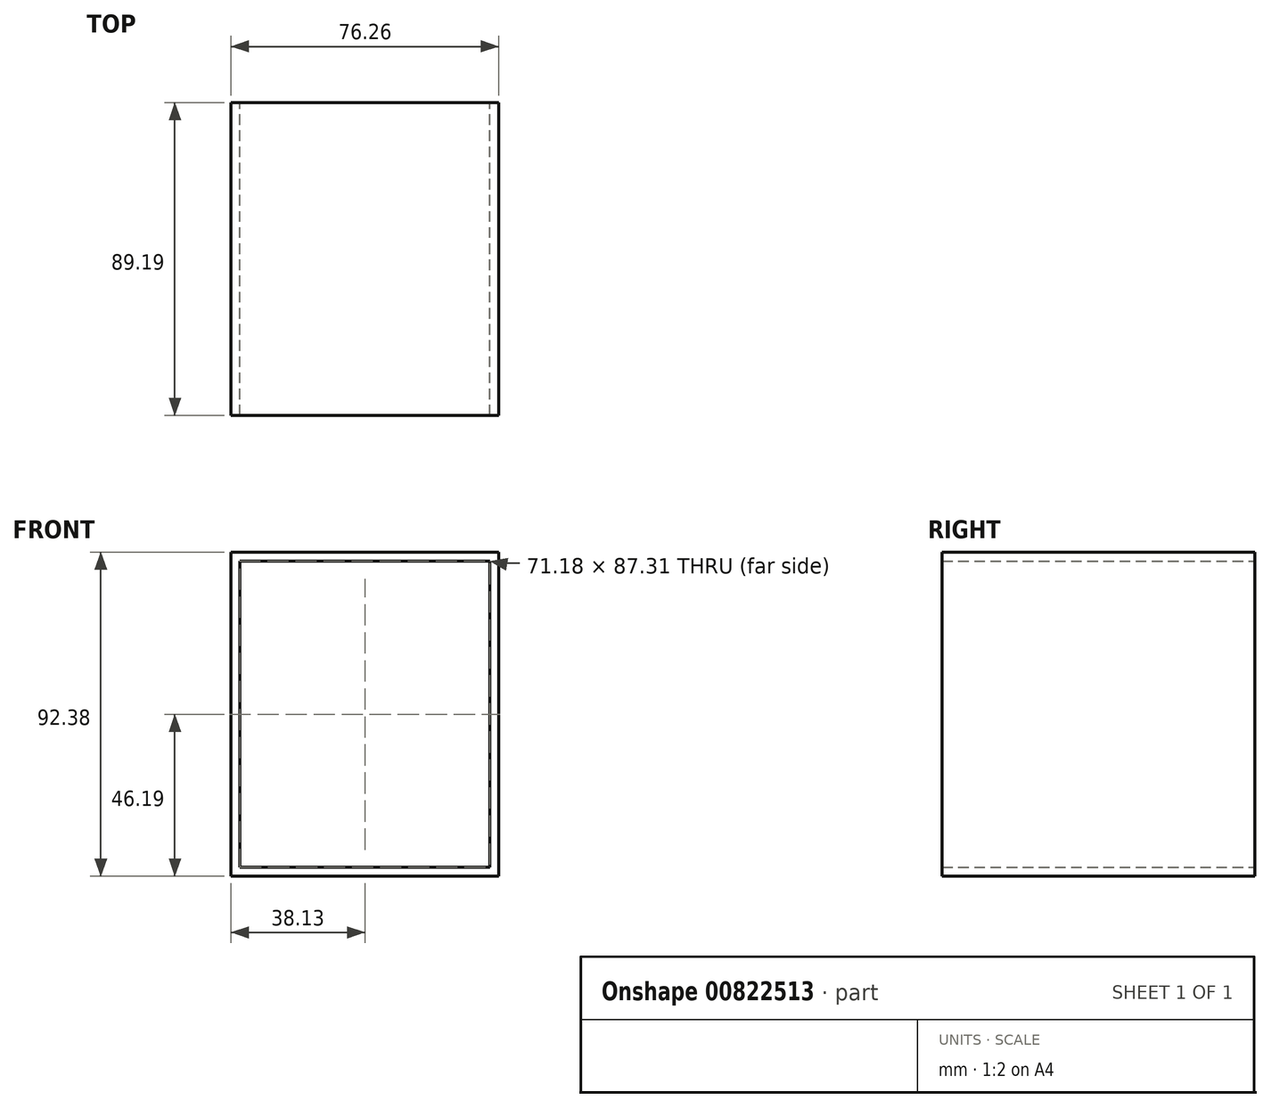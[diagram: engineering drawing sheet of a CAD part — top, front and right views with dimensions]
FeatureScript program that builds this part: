
annotation { "Feature Type Name" : "Feature", "Feature Type Description" : "" }
export const myFeature = defineFeature(function(context is Context, id is Id, definition is map)
    precondition{}
    {
        {
            var Q0;
            Q0=qCreatedBy(makeId("Front.planeOp"),FACE);
            var sketch = newSketch(context, id + "F0", { "sketchPlane" : qUnion([Q0])});
            skLineSegment(sketch, "E0.bottom", {"start": v(38.13, -46.2) * mm, "end": v(-38.13, -46.2) * mm});
            skLineSegment(sketch, "E0.top", {"start": v(38.13, 46.2) * mm, "end": v(-38.13, 46.2) * mm});
            skLineSegment(sketch, "E0.left", {"start": v(38.13, -46.2) * mm, "end": v(38.13, 46.2) * mm});
            skLineSegment(sketch, "E0.right", {"start": v(-38.13, -46.2) * mm, "end": v(-38.13, 46.2) * mm});
            skPoint(sketch, "E0.middle", {"position": v(0, 0) * mm});
            skLineSegment(sketch, "E1.bottom", {"start": v(20.07, 13.05) * mm, "end": v(-20.07, 13.05) * mm, "construction": true});
            skLineSegment(sketch, "E1.top", {"start": v(20.07, 79.34) * mm, "end": v(-20.07, 79.34) * mm, "construction": true});
            skLineSegment(sketch, "E1.left", {"start": v(20.07, 13.05) * mm, "end": v(20.07, 79.34) * mm, "construction": true});
            skLineSegment(sketch, "E1.right", {"start": v(-20.07, 13.05) * mm, "end": v(-20.07, 79.34) * mm, "construction": true});
            skPoint(sketch, "E1.middle", {"position": v(0, 46.2) * mm});
            skSolve(sketch);
        }
        {
            var Q0;
            Q0 = qSketchRegion(id + "F0", true);
            extrude(context, id + "F1", {"entities" : qUnion([Q0]), "depth" : 89.19 * mm, "offsetDistance" : 25.4 * mm});
        }
        {
            var Q0;
            Q0=makeQuery(id+"F1.opExtrude","CAP_FACE",FACE,{"disambiguationData":[OSD([sQuery(id+"F0.wireOp",EDGE,"E0.bottom"),sQuery(id+"F0.wireOp",EDGE,"E0.top"),sQuery(id+"F0.wireOp",EDGE,"E0.left"),sQuery(id+"F0.wireOp",EDGE,"E0.right")])],"isStart":false});
            var Q1;
            Q1=makeQuery(id+"F1.opExtrude","CAP_FACE",FACE,{"disambiguationData":[OSD([sQuery(id+"F0.wireOp",EDGE,"E0.bottom"),sQuery(id+"F0.wireOp",EDGE,"E0.top"),sQuery(id+"F0.wireOp",EDGE,"E0.left"),sQuery(id+"F0.wireOp",EDGE,"E0.right")])],"isStart":true});
            shell(context, id + "F2", {"entities" : qUnion([Q0, Q1]), "thickness" : 2.54 * mm});
        }
    });
